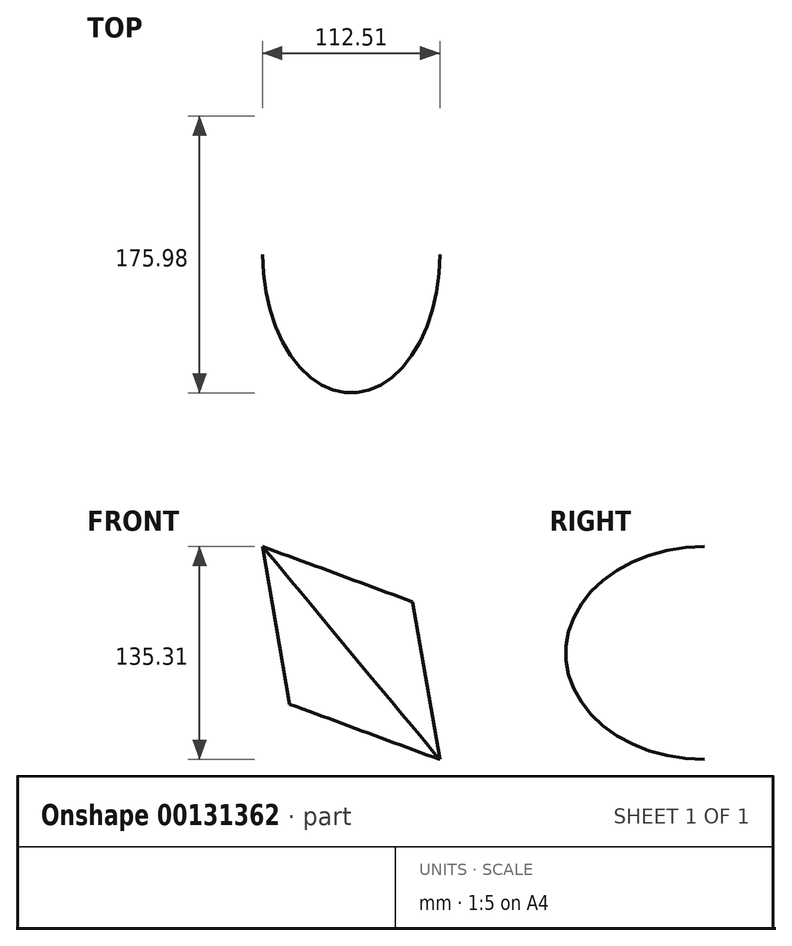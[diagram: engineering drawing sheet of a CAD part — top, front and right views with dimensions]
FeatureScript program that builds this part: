
annotation { "Feature Type Name" : "Feature", "Feature Type Description" : "" }
export const myFeature = defineFeature(function(context is Context, id is Id, definition is map)
    precondition{}
    {
        {
            var Q0;
            Q0=qCreatedBy(makeId("Front.planeOp"),FACE);
            var sketch = newSketch(context, id + "F0", { "sketchPlane" : qUnion([Q0])});
            skCircle(sketch, "E0.cCircle", {"center": v(0, 0) * mm, "radius": 29.33 * mm, "construction": true});
            skLineSegment(sketch, "E0.0", {"start": v(-57.81, -9.93) * mm, "end": v(20.31, 55.03) * mm});
            skLineSegment(sketch, "E0.1", {"start": v(20.31, 55.03) * mm, "end": v(37.5, -45.1) * mm});
            skLineSegment(sketch, "E0.2", {"start": v(37.5, -45.1) * mm, "end": v(-57.81, -9.93) * mm});
            skPoint(sketch, "E0.0.midPoint", {"position": v(-18.75, 22.55) * mm});
            skSolve(sketch);
        }
        {
            var Q0;
            Q0=makeQuery(id+"F0.imprint","IMPRINT",FACE,{"disambiguationData":[TD([[makeQuery(id+"F0.imprint","IMPRINT",EDGE,{"derivedFrom":sQuery(id+"F0.wireOp",EDGE,"E0.0")}),-1.0]])]});
            var Q1;
            Q1=sQuery(id+"F0.wireOp",EDGE,"E0.0");
            revolve(context, id + "F1", {"entities" : qUnion([Q0]), "axis" : qUnion([Q1]), "revolveType" : RevolveType.FULL});
        }
    });
